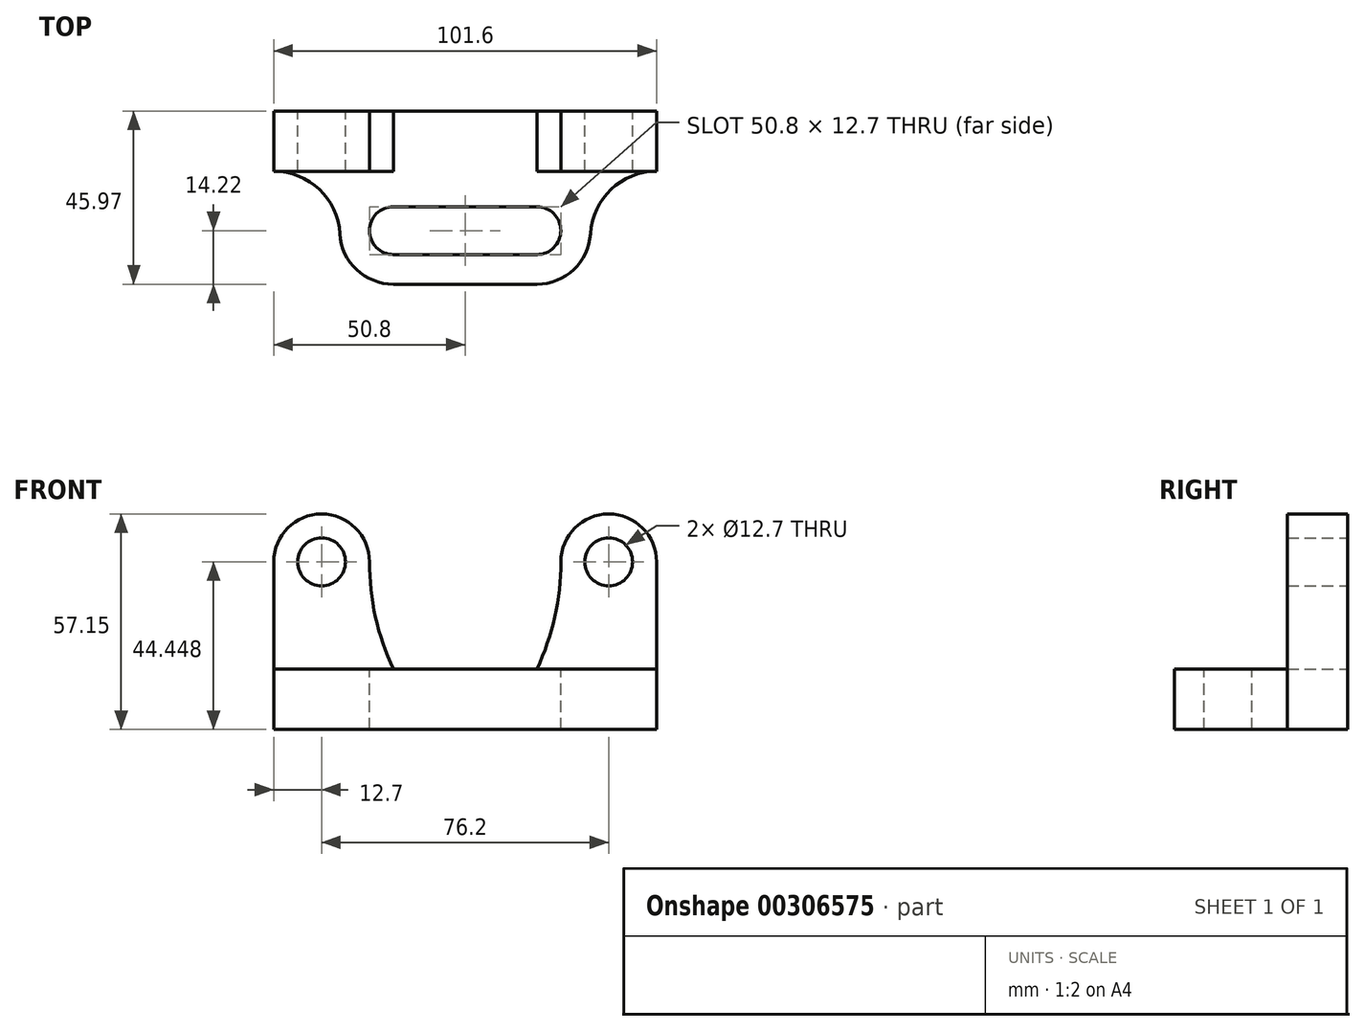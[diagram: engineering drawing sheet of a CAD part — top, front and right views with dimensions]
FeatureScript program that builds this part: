
annotation { "Feature Type Name" : "Feature", "Feature Type Description" : "" }
export const myFeature = defineFeature(function(context is Context, id is Id, definition is map)
    precondition{}
    {
        {
            var Q0;
            Q0=qCreatedBy(makeId("Front.planeOp"),FACE);
            var sketch = newSketch(context, id + "F0", { "sketchPlane" : qUnion([Q0])});
            skLineSegment(sketch, "E0", {"start": v(0, 0) * mm, "end": v(0, 28.45) * mm});
            skArc(sketch, "E1", {"start": v(25.4, 28.45) * mm, "mid": v(12.7, 41.15) * mm, "end": v(0, 28.45) * mm});
            skLineSegment(sketch, "E2", {"start": v(31.75, 0) * mm, "end": v(69.85, 0) * mm});
            skArc(sketch, "E3", {"start": v(101.6, 28.45) * mm, "mid": v(88.9, 41.15) * mm, "end": v(76.2, 28.45) * mm});
            skLineSegment(sketch, "E4", {"start": v(101.6, 28.45) * mm, "end": v(101.6, 0) * mm});
            skLineSegment(sketch, "E5", {"start": v(101.6, 0) * mm, "end": v(0, 0) * mm});
            skLineSegment(sketch, "E6", {"start": v(101.6, 0) * mm, "end": v(101.6, -16) * mm});
            skLineSegment(sketch, "E7", {"start": v(101.6, -16) * mm, "end": v(0, -16) * mm});
            skLineSegment(sketch, "E8", {"start": v(0, -16) * mm, "end": v(0, 0) * mm});
            skCircle(sketch, "E9", {"center": v(88.9, 28.45) * mm, "radius": 6.35 * mm});
            skCircle(sketch, "E10", {"center": v(12.7, 28.45) * mm, "radius": 6.35 * mm});
            skArc(sketch, "E11", {"start": v(69.85, 0) * mm, "mid": v(74.6, 13.87) * mm, "end": v(76.2, 28.45) * mm});
            skArc(sketch, "E12", {"start": v(25.4, 28.45) * mm, "mid": v(27, 13.87) * mm, "end": v(31.75, 0) * mm});
            skSolve(sketch);
        }
        {
            var Q0;
            Q0=makeQuery(id+"F0.imprint","IMPRINT",FACE,{"disambiguationData":[TD([[makeQuery(id+"F0.imprint","IMPRINT",EDGE,{"derivedFrom":sQuery(id+"F0.wireOp",EDGE,"E3")}),1.0]])]});
            var Q1;
            {var subQ0=sQuery(id+"F0.wireOp",EDGE,"E0");Q1=makeQuery(id+"F0.imprint","IMPRINT",FACE,{"disambiguationData":[TD([[makeQuery(id+"F0.imprint","IMPRINT",EDGE,{"derivedFrom":subQ0}),-1.0]])]});}
            extrude(context, id + "F1", {"entities" : qUnion([Q0, Q1]), "depth" : 16 * mm});
        }
        {
            var Q0;
            {var subQ0=sQuery(id+"F0.wireOp",EDGE,"E6");Q0=makeQuery(id+"F0.imprint","IMPRINT",FACE,{"disambiguationData":[TD([[makeQuery(id+"F0.imprint","IMPRINT",EDGE,{"derivedFrom":subQ0}),-1.0]])]});}
            extrude(context, id + "F2", {"entities" : qUnion([Q0]), "operationType" : NewBodyOperationType.ADD, "depth" : 45.97 * mm});
        }
        {
            var Q0;
            Q0=makeQuery(id+"F2.opExtrude","SWEPT_FACE",FACE,{"disambiguationData":[OSD([sQuery(id+"F0.wireOp",EDGE,"E5")])]});
            var sketch = newSketch(context, id + "F3", { "sketchPlane" : qUnion([Q0])});
            skLineSegment(sketch, "E13", {"start": v(31.75, -31.75) * mm, "end": v(69.85, -31.75) * mm, "construction": true});
            skArc(sketch, "E14", {"start": v(69.85, -38.1) * mm, "mid": v(76.2, -31.75) * mm, "end": v(69.85, -25.4) * mm});
            skArc(sketch, "E15", {"start": v(31.75, -25.4) * mm, "mid": v(25.4, -31.75) * mm, "end": v(31.75, -38.1) * mm});
            skLineSegment(sketch, "E16", {"start": v(31.75, -25.4) * mm, "end": v(69.85, -25.4) * mm});
            skLineSegment(sketch, "E17", {"start": v(31.75, -38.1) * mm, "end": v(69.85, -38.1) * mm});
            skArc(sketch, "E18", {"start": v(17.55, -32.57) * mm, "mid": v(21.99, -42.1) * mm, "end": v(31.75, -45.97) * mm});
            skArc(sketch, "E19", {"start": v(17.55, -32.57) * mm, "mid": v(12.07, -20.8) * mm, "end": v(0, -16) * mm});
            skArc(sketch, "E20", {"start": v(69.85, -45.97) * mm, "mid": v(79.61, -42.1) * mm, "end": v(84.05, -32.57) * mm});
            skArc(sketch, "E21", {"start": v(101.6, -16) * mm, "mid": v(89.53, -20.8) * mm, "end": v(84.05, -32.57) * mm});
            skSolve(sketch);
        }
        {
            var Q0;
            {var subQ0=sQuery(id+"F3.wireOp",EDGE,"E18");Q0=makeQuery(id+"F3.imprint","IMPRINT",FACE,{"disambiguationData":[TD([[makeQuery(id+"F3.imprint","IMPRINT",EDGE,{"derivedFrom":subQ0}),-1.0]])]});}
            var Q1;
            {var subQ0=sQuery(id+"F3.wireOp",EDGE,"E20");Q1=makeQuery(id+"F3.imprint","IMPRINT",FACE,{"disambiguationData":[TD([[makeQuery(id+"F3.imprint","IMPRINT",EDGE,{"derivedFrom":subQ0}),-1.0]])]});}
            extrude(context, id + "F4", {"entities" : qUnion([Q0, Q1]), "operationType" : NewBodyOperationType.REMOVE, "oppositeDirection" : true, "depth" : 25.4 * mm});
        }
        {
            var Q0;
            Q0=makeQuery(id+"F3.imprint","IMPRINT",FACE,{"disambiguationData":[TD([[makeQuery(id+"F3.imprint","IMPRINT",EDGE,{"derivedFrom":sQuery(id+"F3.wireOp",EDGE,"E14")}),1.0]])]});
            extrude(context, id + "F5", {"entities" : qUnion([Q0]), "operationType" : NewBodyOperationType.REMOVE, "oppositeDirection" : true, "depth" : 25.4 * mm});
        }
    });
